# Revit family: IS_Connect_E7112_BIM_DE
name_source: partatom
category: Plumbing Fixtures
revit_build: Autodesk Revit MEP 2014 (Build: 20130308_1515(x64)
units: mm (PartAtom-declared; Revit-internal decimal feet)

## types (1)
- E711201 - Connect full pedestal
    Accessories = www.idealstandard.de\ersatzteile
    AreaUnits = millimeters
    Assembly Code = C1030200
    AssetType = Fixed
    BIMObjectName = ISI_IdealStandard_PedestalWashBasins_Connect_E711201
    BarCode = 5017830399032
    Brand = Ideal Standard
    CWFU = 0
    Color = white
    ConnectionType = Plumbing
    Cost = 0 $
    Default Elevation = 850 mm  [stored 2.78871 ft]
    Description = E711201 Connect full pedestal
    DrainSize = 0 mm  [stored 0 ft]
    DurationUnit = year
    ExpectedLife = 25
    Features = Connect full pedestal
    Finish = white
    GrossWeight = 0
    HWFU = 0
    IfcExportAs = IfcSanitaryType
    IfcExportType = WASHHANDBASIN
    InstallationInstructions = www.idealstandard.de\produkte
    LinearUnits = millimeters
    ManufacturerURL = www.idealstandard.de
    Material = Vitreous china
    Model = E711201
    ModelNumber = E711201
    ModelReference = Connect full pedestal
    NBSDescription = Pedestal wash basins
    NBSReference = 45-35-70/365
    Name = PedestalWashBasins_Connect_E711201_IdealStandard
    NettWeight = 10,702 kg
    NominalHeight = 720 mm
    NominalLength = 188 mm
    NominalWidth = 193 mm
    ProductInformation = www.idealstandard.de\produkte
    Shape = Sculptured
    Size = 193x188x720mm
    Space = Internal
    URL = www.idealstandard.com
    Uniclass2015Code = Pr_40_20_96_63
    Uniclass2015Title = Pedestal wash basins
    Uniclass2015Version = Products v1.1
    Version = 1
    VolumeUnits = Litres
    WFU = 0
    WarrantyDescription = Manufacturers Warranty
    WarrantyDurationUnit = year
    WashHandBasinMounting = i.e.Wall Hung
    WashHandBasinType = Hand Rinse

note: [stored X ft] marks values corroborated as IEEE doubles in the binary element streams (Revit-internal decimal feet)

## geometry (parser evidence)
native form markers: Sweep x2
no freeform markers — native parametric forms only
